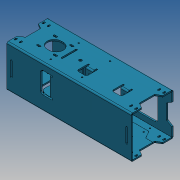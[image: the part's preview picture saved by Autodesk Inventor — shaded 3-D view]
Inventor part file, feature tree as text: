
AUTODESK INVENTOR PART (.ipt)
format: ipt  version: 2017 (Build 210142000, 142)  size: 979,456 bytes
history: native  units: mm
features: other x14, sketch x4, extrude x2, mirror x2, projected_geometry x2, plane x1
ambient origin geometry x8: Origin, YZ Plane, XZ Plane, XY Plane, X Axis, Y Axis, Z Axis, Center Point
bodies: Body1 (feature_tree)
feature tree (25):
  other  "Sólido1"
  sketch  "Boceto1"  dims[d1=56.4mm d2=72.0mm]
  extrude  "Extrusión1"  Depth=72.0mm
  other  "Pliegue2"
  other  "Pliegue4"
  sketch  "Boceto4"  dims[d4=200.0mm d5=42.0mm]
  other  "Cara1"
  other  "Pliegue3"
  mirror  "Simetría2"
  sketch  "Boceto5"  dims[d6=8.0mm]
  other  "Cara4"
  other  "Cara5"
  plane  "Plano de trabajo1"
  mirror  "Simetría1"
  other  "Pliegue5"
  extrude  "Extrusión6"  Depth=42.0mm
  other  "Placa2"
  other  "Doblez2"
  projected_geometry  "Contorno proyectado6"
  other  "Placa5"
  other  "Doblez5"
  other  "Placa6"
  other  "Doblez6"
  sketch  "Boceto7"  dims[d8=5.0mm d9=41.14mm d10=6.0mm d11=53.14mm d12=6.0mm d13=4.0mm d14=100.0mm d15=20.0mm d16=80.0mm d17=60.0mm d18=4.0mm d19=33.93mm d20=22.0mm d21=120.0mm d22=130.0mm d23=20.0mm d24=4.0mm d25=0.0mm d42=47.14mm d43=47.14mm d44=20.0mm d45=6.0mm d46=14.2mm d47=25.0mm d48=0.1mm d49=4.0mm d50=2.0mm d51=8.0mm d52=4.0mm d62=4.4mm d63=41.0mm d70=4.4mm d71=130.7mm d86=50.0mm d87=355.0mm d88=12.5mm d89=12.5mm d90=23.6mm d91=11.8mm d97=190.1mm d134=4.0mm d135=2.0mm d136=8.0mm d137=4.0mm d138=90.0deg d139=0.1mm d142=10.0mm d143=4.0mm d144=80.0mm d145=5.0mm d146=60.0deg d155=60.0deg d156=41.0mm d159=60.0deg d160=112.0mm d161=60.0deg d162=2.0mm d163=6.0mm d165=4.0mm d166=33.0mm d168=15.0mm d169=60.0mm d171=30.0mm d172=4.0mm d173=21.0mm d174=10.5mm d175=4.0mm d176=2.0mm d177=8.0mm d178=4.0mm d179=90.0deg d180=0.5mm d181=8.0mm d182=15.0mm d183=4.0mm d184=8.0mm d185=2.0mm d186=21.0mm d187=10.5mm d188=20.0mm d189=8.0mm d190=20.0mm d192=100.0mm d193=10.0mm d195=10.0mm d197=120.0mm d198=4.0mm d199=2.0mm d200=8.0mm d201=4.0mm d202=90.0deg d203=0.1mm d204=25.0mm d205=25.0mm d206=6.0mm d207=62.8mm d209=2.0mm d210=8.0mm d211=10.0mm d212=50.0mm d215=4.0mm d216=18.0mm d217=12.0mm d218=1.0mm d219=21.0mm d220=8.0mm d221=0.1mm d222=1.0mm d224=0.1mm d225=4.2mm d226=12.0mm d227=4.2mm d228=4.2mm d229=50.0mm d230=75.0mm d233=0.1mm d234=0.3mm d237=17.4mm d238=1.0mm d239=0.1mm d240=0.1mm d241=4.0mm d242=2.0mm d243=8.0mm d244=4.0mm d245=0.1mm d246=4.0mm d247=2.0mm d248=8.0mm d249=4.0mm d250=4.0mm d251=2.0mm d252=8.0mm d253=4.0mm d254=90.0deg d255=0.1mm d256=10.0mm d257=0.0mm d258=20.0mm d259=3.0mm d260=4.0mm d261=0.05mm d262=152.0mm d263=18.0mm d264=18.0mm d265=18.0mm d266=18.0mm d267=0.1mm d268=0.1mm d269=120.0deg d270=20.0mm d271=4.0mm]
  projected_geometry  "Contorno proyectado7"
